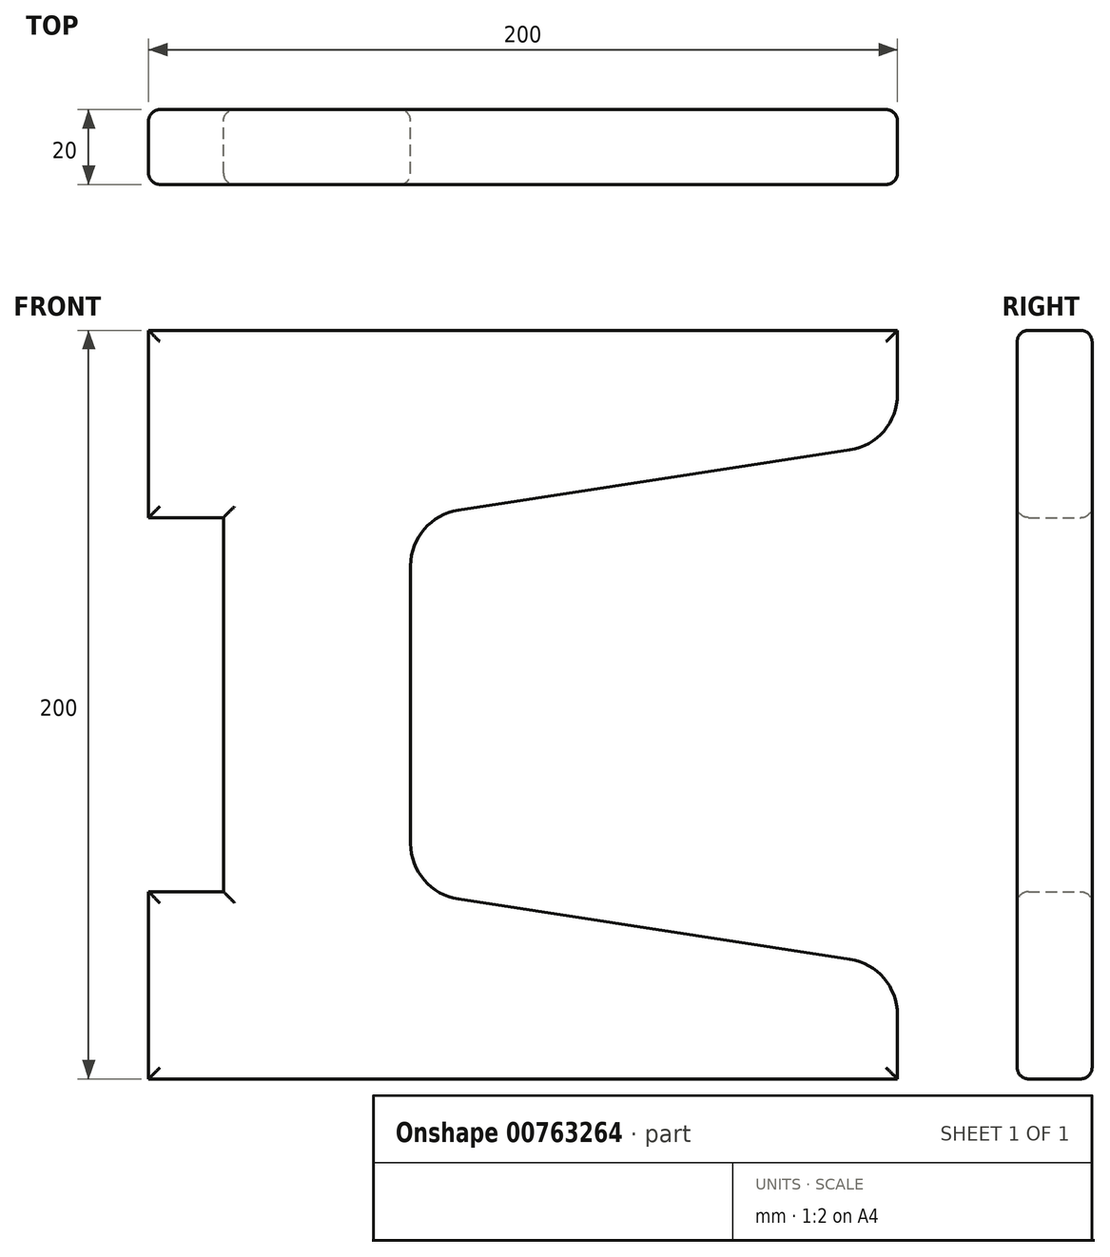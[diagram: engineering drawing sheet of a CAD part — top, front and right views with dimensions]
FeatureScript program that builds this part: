
annotation { "Feature Type Name" : "Feature", "Feature Type Description" : "" }
export const myFeature = defineFeature(function(context is Context, id is Id, definition is map)
    precondition{}
    {
        {
            var Q0;
            Q0=qCreatedBy(makeId("Front.planeOp"),FACE);
            var sketch = newSketch(context, id + "F0", { "sketchPlane" : qUnion([Q0])});
            skLineSegment(sketch, "E0", {"start": v(0, 0) * mm, "end": v(0, 50) * mm});
            skLineSegment(sketch, "E1", {"start": v(0, 200) * mm, "end": v(200, 200) * mm});
            skLineSegment(sketch, "E2", {"start": v(200, 200) * mm, "end": v(200, 182.87) * mm});
            skLineSegment(sketch, "E3", {"start": v(187.28, 168.04) * mm, "end": v(82.72, 151.96) * mm});
            skLineSegment(sketch, "E4", {"start": v(70, 137.13) * mm, "end": v(70, 62.87) * mm});
            skLineSegment(sketch, "E5", {"start": v(82.72, 48.04) * mm, "end": v(187.28, 31.96) * mm});
            skLineSegment(sketch, "E6", {"start": v(200, 17.13) * mm, "end": v(200, 0) * mm});
            skLineSegment(sketch, "E7", {"start": v(200, 0) * mm, "end": v(0, 0) * mm});
            skPoint(sketch, "E8.visualSharp", {"position": v(200, 170) * mm});
            skArc(sketch, "E8.filletArc", {"start": v(187.28, 168.04) * mm, "mid": v(196.38, 173.1) * mm, "end": v(200, 182.87) * mm});
            skPoint(sketch, "E9.visualSharp", {"position": v(200, 30) * mm});
            skArc(sketch, "E9.filletArc", {"start": v(200, 17.13) * mm, "mid": v(196.38, 26.9) * mm, "end": v(187.28, 31.96) * mm});
            skPoint(sketch, "E10.visualSharp", {"position": v(70, 50) * mm});
            skArc(sketch, "E10.filletArc", {"start": v(70, 62.87) * mm, "mid": v(73.62, 53.1) * mm, "end": v(82.72, 48.04) * mm});
            skPoint(sketch, "E11.visualSharp", {"position": v(70, 150) * mm});
            skArc(sketch, "E11.filletArc", {"start": v(82.72, 151.96) * mm, "mid": v(73.62, 146.9) * mm, "end": v(70, 137.13) * mm});
            skLineSegment(sketch, "E12", {"start": v(0, 200) * mm, "end": v(0, 150) * mm});
            skLineSegment(sketch, "E13", {"start": v(0, 150) * mm, "end": v(20, 150) * mm});
            skLineSegment(sketch, "E14", {"start": v(20, 150) * mm, "end": v(20, 50) * mm});
            skLineSegment(sketch, "E15", {"start": v(20, 50) * mm, "end": v(0, 50) * mm});
            skSolve(sketch);
        }
        {
            var Q0;
            Q0=makeQuery(id+"F0.imprint","IMPRINT",FACE,{"disambiguationData":[TD([[makeQuery(id+"F0.imprint","IMPRINT",EDGE,{"derivedFrom":sQuery(id+"F0.wireOp",EDGE,"E0")}),-1.0]])]});
            extrude(context, id + "F1", {"entities" : qUnion([Q0]), "depth" : 20 * mm, "offsetDistance" : 25 * mm});
        }
        {
            var Q0;
            Q0=makeQuery(id+"F1.opExtrude","CAP_FACE",FACE,{"disambiguationData":[OSD([sQuery(id+"F0.wireOp",EDGE,"E0"),sQuery(id+"F0.wireOp",EDGE,"E1"),sQuery(id+"F0.wireOp",EDGE,"E2"),sQuery(id+"F0.wireOp",EDGE,"E3"),sQuery(id+"F0.wireOp",EDGE,"E4"),sQuery(id+"F0.wireOp",EDGE,"E5"),sQuery(id+"F0.wireOp",EDGE,"E6"),sQuery(id+"F0.wireOp",EDGE,"E7"),sQuery(id+"F0.wireOp",EDGE,"E8.filletArc"),sQuery(id+"F0.wireOp",EDGE,"E9.filletArc"),sQuery(id+"F0.wireOp",EDGE,"E10.filletArc"),sQuery(id+"F0.wireOp",EDGE,"E11.filletArc"),sQuery(id+"F0.wireOp",EDGE,"E12"),sQuery(id+"F0.wireOp",EDGE,"E13"),sQuery(id+"F0.wireOp",EDGE,"E14"),sQuery(id+"F0.wireOp",EDGE,"E15")])],"isStart":false});
            var Q1;
            Q1=makeQuery(id+"F1.opExtrude","CAP_FACE",FACE,{"disambiguationData":[OSD([sQuery(id+"F0.wireOp",EDGE,"E0"),sQuery(id+"F0.wireOp",EDGE,"E1"),sQuery(id+"F0.wireOp",EDGE,"E2"),sQuery(id+"F0.wireOp",EDGE,"E3"),sQuery(id+"F0.wireOp",EDGE,"E4"),sQuery(id+"F0.wireOp",EDGE,"E5"),sQuery(id+"F0.wireOp",EDGE,"E6"),sQuery(id+"F0.wireOp",EDGE,"E7"),sQuery(id+"F0.wireOp",EDGE,"E8.filletArc"),sQuery(id+"F0.wireOp",EDGE,"E9.filletArc"),sQuery(id+"F0.wireOp",EDGE,"E10.filletArc"),sQuery(id+"F0.wireOp",EDGE,"E11.filletArc"),sQuery(id+"F0.wireOp",EDGE,"E12"),sQuery(id+"F0.wireOp",EDGE,"E13"),sQuery(id+"F0.wireOp",EDGE,"E14"),sQuery(id+"F0.wireOp",EDGE,"E15")])],"isStart":true});
            fillet(context, id + "F2", {"entities" : qUnion([Q0, Q1]), "radius" : 3 * mm, "tangentPropagation" : true, "allowEdgeOverflow" : false});
        }
        {
            var Q0;
            Q0=makeQuery(id+"F1.opExtrude","SWEPT_FACE",FACE,{"disambiguationData":[OSD([sQuery(id+"F0.wireOp",EDGE,"E1")])]});
            var sketch = newSketch(context, id + "F3", { "sketchPlane" : qUnion([Q0])});
            skLineSegment(sketch, "E16", {"start": v(0, -10) * mm, "end": v(90, -10) * mm});
            skSolve(sketch);
        }
        {
            var Q0;
            Q0=makeQuery(id+"F1.opExtrude","SWEPT_FACE",FACE,{"disambiguationData":[OSD([sQuery(id+"F0.wireOp",EDGE,"E7")])]});
            var sketch = newSketch(context, id + "F4", { "sketchPlane" : qUnion([Q0])});
            skLineSegment(sketch, "E17", {"start": v(0, 10) * mm, "end": v(90, 10) * mm});
            skSolve(sketch);
        }
    });
